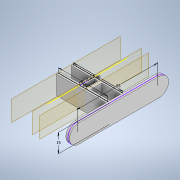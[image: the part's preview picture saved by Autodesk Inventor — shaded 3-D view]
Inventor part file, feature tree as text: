
AUTODESK INVENTOR PART (.ipt)
format: ipt  version: 2020.3 (Build 243373000, 373)  size: 155,648 bytes
history: native  units: mm
features: sketch x5, plane x5, extrude x5
ambient origin geometry x8: Origin, YZ Plane, XZ Plane, XY Plane, X Axis, Y Axis, Z Axis, Center Point
bodies: Solid1 (feature_tree)
feature tree (15):
  sketch  "Sketch1"  dims[d25=65.0mm d26=15.0mm]
  plane  "Work Plane1"
  plane  "Work Plane2"
  extrude  "Extrusion1"  Depth=15.0mm
  sketch  "Sketch2"  dims[d27=6.0mm d28=3.0mm d29=0.0mm]
  sketch  "Sketch3"  dims[d30=40.0mm d31=3.0mm]
  plane  "Work Plane5"
  plane  "Work Plane6"
  plane  "Work Plane7"
  sketch  "Sketch5"  dims[d32=3.0mm d35=40.0mm]
  sketch  "Sketch6"  dims[d39=-18.5mm d42=6.0mm d43=6.0mm d44=6.0mm d45=3.0mm d46=0.0mm d47=3.0mm d48=0.0mm d49=3.0mm d50=0.0mm d51=3.0mm d52=0.0mm d4=0.5mm d5=0.872665mm d6=0.5mm d7=0.872665mm]
  extrude  "Extrusion2"  Depth=3.0mm TaperAngle=0.0deg
  extrude  "Extrusion3"  Depth=3.0mm
  extrude  "Extrusion4"  Depth=40.0mm
  extrude  "Extrusion5"  Depth=6.0mm
